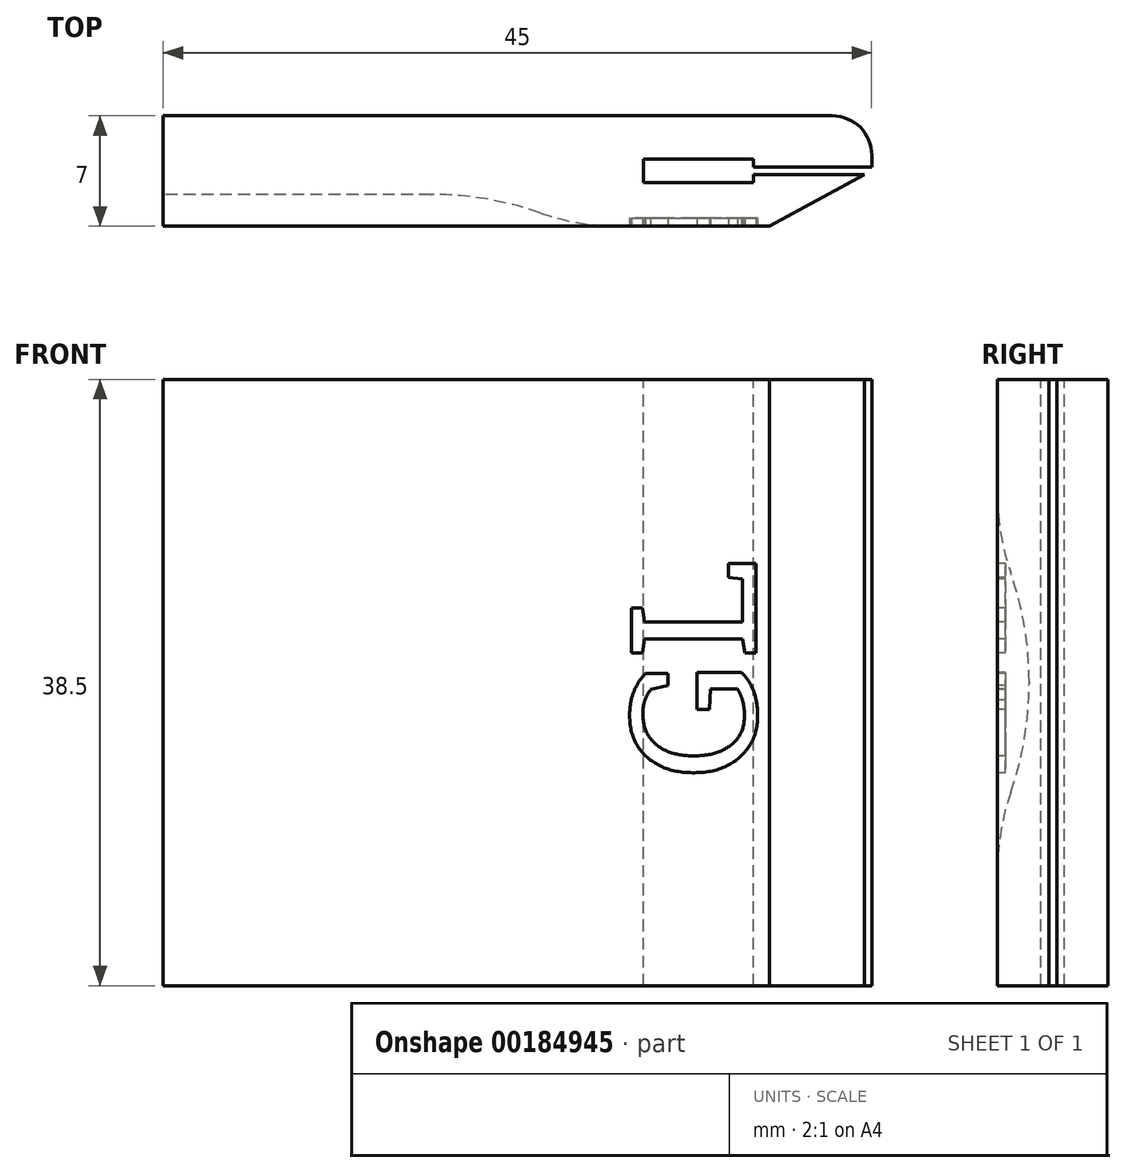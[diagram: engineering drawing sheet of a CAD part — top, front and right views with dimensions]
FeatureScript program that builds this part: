
annotation { "Feature Type Name" : "Feature", "Feature Type Description" : "" }
export const myFeature = defineFeature(function(context is Context, id is Id, definition is map)
    precondition{}
    {
        {
            var Q0;
            Q0=qCreatedBy(makeId("Top.planeOp"),FACE);
            var sketch = newSketch(context, id + "F0", { "sketchPlane" : qUnion([Q0])});
            skLineSegment(sketch, "E0.bottom", {"start": v(-22.94, 8.97) * mm, "end": v(22.06, 8.97) * mm});
            skLineSegment(sketch, "E0.top", {"start": v(-22.94, 1.97) * mm, "end": v(22.06, 1.97) * mm});
            skLineSegment(sketch, "E0.left", {"start": v(-22.94, 8.97) * mm, "end": v(-22.94, 1.97) * mm});
            skLineSegment(sketch, "E0.right", {"start": v(22.06, 8.97) * mm, "end": v(22.06, 1.97) * mm});
            skSolve(sketch);
        }
        {
            var Q0;
            Q0=makeQuery(id+"F0.imprint","IMPRINT",FACE,{"disambiguationData":[TD([[makeQuery(id+"F0.imprint","IMPRINT",EDGE,{"derivedFrom":sQuery(id+"F0.wireOp",EDGE,"E0.bottom")}),-1.0]])]});
            extrude(context, id + "F1", {"entities" : qUnion([Q0]), "depth" : 38.5 * mm});
        }
        {
            var Q0;
            Q0=makeQuery(id+"F1.opExtrude","SWEPT_EDGE",EDGE,{"disambiguationData":[OSD([sQuery(id+"F0.wireOp",EDGE,"E0.top"),sQuery(id+"F0.wireOp",EDGE,"E0.right")])]});
            chamfer(context, id + "F2", {"entities" : qUnion([Q0]), "chamferType" : ChamferType.TWO_OFFSETS, "width1" : 3.5 * mm, "oppositeDirection" : false, "width2" : 6.5 * mm, "tangentPropagation" : true});
        }
        {
            var Q0;
            Q0=makeQuery(id+"F1.opExtrude","SWEPT_EDGE",EDGE,{"disambiguationData":[OSD([sQuery(id+"F0.wireOp",EDGE,"E0.bottom"),sQuery(id+"F0.wireOp",EDGE,"E0.right")])]});
            fillet(context, id + "F3", {"entities" : qUnion([Q0]), "radius" : 2.5 * mm, "tangentPropagation" : true, "allowEdgeOverflow" : false});
        }
        {
            var Q0;
            Q0=makeQuery(id+"F1.opExtrude","SWEPT_FACE",FACE,{"disambiguationData":[OSD([sQuery(id+"F0.wireOp",EDGE,"E0.top")])]});
            var sketch = newSketch(context, id + "F4", { "sketchPlane" : qUnion([Q0])});
            skLineSegment(sketch, "E1.bottom", {"start": v(-22.94, 28.25) * mm, "end": v(3.06, 28.25) * mm});
            skLineSegment(sketch, "E1.top", {"start": v(-22.94, 10.25) * mm, "end": v(3.06, 10.25) * mm});
            skLineSegment(sketch, "E1.left", {"start": v(-22.94, 28.25) * mm, "end": v(-22.94, 10.25) * mm});
            skLineSegment(sketch, "E1.right", {"start": v(3.06, 28.25) * mm, "end": v(3.06, 10.25) * mm});
            skLineSegment(sketch, "E2", {"start": v(3.06, 19.25) * mm, "end": v(-22.94, 19.25) * mm, "construction": true});
            skSolve(sketch);
        }
        {
            var Q0;
            Q0=makeQuery(id+"F4.imprint","IMPRINT",FACE,{"disambiguationData":[TD([[makeQuery(id+"F4.imprint","IMPRINT",EDGE,{"derivedFrom":sQuery(id+"F4.wireOp",EDGE,"E1.bottom")}),-1.0]])]});
            extrude(context, id + "F5", {"entities" : qUnion([Q0]), "operationType" : NewBodyOperationType.REMOVE, "oppositeDirection" : true, "depth" : 2 * mm});
        }
        {
            var Q0;
            Q0=makeQuery(id+"F5.boolean.opBoolean","COPY",EDGE,{"derivedFrom":makeQuery(id+"F5.opExtrude","SWEPT_EDGE",EDGE,{"disambiguationData":[OSD([sQuery(id+"F4.wireOp",EDGE,"E1.bottom"),sQuery(id+"F4.wireOp",EDGE,"E1.right")])]})});
            var Q1;
            Q1=makeQuery(id+"F5.boolean.opBoolean","COPY",EDGE,{"derivedFrom":makeQuery(id+"F5.opExtrude","SWEPT_EDGE",EDGE,{"disambiguationData":[OSD([sQuery(id+"F4.wireOp",EDGE,"E1.top"),sQuery(id+"F4.wireOp",EDGE,"E1.right")])]})});
            fillet(context, id + "F6", {"entities" : qUnion([Q0, Q1]), "radius" : 9 * mm, "tangentPropagation" : true, "allowEdgeOverflow" : false});
        }
        {
            var Q0;
            Q0=makeQuery(id+"F5.boolean.opBoolean","COPY",EDGE,{"derivedFrom":makeQuery(id+"F5.opExtrude","CAP_EDGE",EDGE,{"disambiguationData":[OSD([sQuery(id+"F4.wireOp",EDGE,"E1.top")])],"isStart":false})});
            fillet(context, id + "F7", {"entities" : qUnion([Q0]), "radius" : 21 * mm, "tangentPropagation" : true, "allowEdgeOverflow" : false});
        }
        {
            var Q0;
            Q0=makeQuery(id+"F1.opExtrude","SWEPT_FACE",FACE,{"disambiguationData":[OSD([sQuery(id+"F0.wireOp",EDGE,"E0.top")])]});
            var Q1;
            Q1=makeQuery(id+"F1.opExtrude","SWEPT_FACE",FACE,{"disambiguationData":[OSD([sQuery(id+"F0.wireOp",EDGE,"E0.bottom")])]});
            cPlane(context, id + "F8", {"entities" : qUnion([Q0, Q1]), "cplaneType" : CPlaneType.MID_PLANE, "offset" : 25 * mm, "width" : 150 * mm, "height" : 150 * mm});
        }
        {
            var Q0;
            Q0=makeQuery(id+"F1.opExtrude","CAP_FACE",FACE,{"disambiguationData":[OSD([sQuery(id+"F0.wireOp",EDGE,"E0.bottom"),sQuery(id+"F0.wireOp",EDGE,"E0.top"),sQuery(id+"F0.wireOp",EDGE,"E0.left"),sQuery(id+"F0.wireOp",EDGE,"E0.right")])],"isStart":false});
            var sketch = newSketch(context, id + "F9", { "sketchPlane" : qUnion([Q0])});
            skLineSegment(sketch, "E3.bottom", {"start": v(14.56, 5.72) * mm, "end": v(22.06, 5.72) * mm});
            skLineSegment(sketch, "E3.top", {"start": v(14.56, 5.22) * mm, "end": v(22.06, 5.22) * mm});
            skLineSegment(sketch, "E3.left", {"start": v(14.56, 5.72) * mm, "end": v(14.56, 5.22) * mm});
            skLineSegment(sketch, "E3.right", {"start": v(22.06, 5.72) * mm, "end": v(22.06, 5.22) * mm});
            skLineSegment(sketch, "E4.bottom", {"start": v(7.56, 6.22) * mm, "end": v(14.56, 6.22) * mm});
            skLineSegment(sketch, "E4.top", {"start": v(7.56, 4.72) * mm, "end": v(14.56, 4.72) * mm});
            skLineSegment(sketch, "E4.left", {"start": v(7.56, 6.22) * mm, "end": v(7.56, 4.72) * mm});
            skLineSegment(sketch, "E4.right", {"start": v(14.56, 6.22) * mm, "end": v(14.56, 4.72) * mm});
            skSolve(sketch);
        }
        {
            var Q0;
            {var subQ3=sQuery(id+"F9.wireOp",EDGE,"E4.bottom");Q0=makeQuery(id+"F9.imprint","IMPRINT",FACE,{"disambiguationData":[TD([[makeQuery(id+"F9.imprint","IMPRINT",EDGE,{"derivedFrom":subQ3}),-1.0]])]});}
            var Q1;
            {var subQ5=sQuery(id+"F9.wireOp",EDGE,"E3.bottom");Q1=makeQuery(id+"F9.imprint","IMPRINT",FACE,{"disambiguationData":[TD([[makeQuery(id+"F9.imprint","IMPRINT",EDGE,{"derivedFrom":subQ5}),-1.0]])]});}
            extrude(context, id + "F10", {"entities" : qUnion([Q0, Q1]), "operationType" : NewBodyOperationType.REMOVE, "endBound" : BoundingType.UP_TO_NEXT, "oppositeDirection" : true, "depth" : 25 * mm});
        }
        {
            var Q0;
            Q0=makeQuery(id+"F7.opFillet","BLEND_EDGE",EDGE,{"disambiguationData":[OD(0.0)],"blendedFrom":[makeQuery(id+"F5.boolean.opBoolean","COPY",EDGE,{"derivedFrom":makeQuery(id+"F5.opExtrude","CAP_EDGE",EDGE,{"disambiguationData":[OSD([sQuery(id+"F4.wireOp",EDGE,"E1.bottom")])],"isStart":false})}),makeQuery(id+"F1.opExtrude","SWEPT_FACE",FACE,{"disambiguationData":[OSD([sQuery(id+"F0.wireOp",EDGE,"E0.top")])]})],"blendedInto":[makeQuery(id+"F1.opExtrude","SWEPT_FACE",FACE,{"disambiguationData":[OSD([sQuery(id+"F0.wireOp",EDGE,"E0.top")])]})]});
            var Q1;
            Q1=makeQuery(id+"FHQU1zlOLmeoFjk_1.1.F7.opFillet","BLEND_EDGE",EDGE,{"blendedFrom":[makeQuery(id+"FHQU1zlOLmeoFjk_1.1.F5.boolean.opBoolean","COPY",EDGE,{"derivedFrom":makeQuery(id+"FHQU1zlOLmeoFjk_1.1.F5.opExtrude","CAP_EDGE",EDGE,{"disambiguationData":[OSD([sQuery(id+"F4.wireOp",EDGE,"E1.bottom")])],"isStart":false})}),makeQuery(id+"F1.opExtrude","SWEPT_FACE",FACE,{"disambiguationData":[OSD([sQuery(id+"F0.wireOp",EDGE,"E0.bottom")])]})],"blendedInto":[makeQuery(id+"F1.opExtrude","SWEPT_FACE",FACE,{"disambiguationData":[OSD([sQuery(id+"F0.wireOp",EDGE,"E0.bottom")])]})]});
            fillet(context, id + "F11", {"entities" : qUnion([Q0, Q1]), "radius" : 15 * mm, "tangentPropagation" : true, "allowEdgeOverflow" : false});
        }
        {
            var Q0;
            Q0=makeQuery(id+"F1.opExtrude","SWEPT_FACE",FACE,{"disambiguationData":[OSD([sQuery(id+"F0.wireOp",EDGE,"E0.top")])]});
            var sketch = newSketch(context, id + "F12", { "sketchPlane" : qUnion([Q0])});
            skText(sketch, "E5", { "text": "GL\n", "fontName": "RobotoSlab-Regular.ttf"});
            const initialGuessF12  = {"E5": [0.0147, 0.01323, 0, 1, 0.008]};
            skSetInitialGuess(sketch, initialGuessF12);
            skSolve(sketch);
        }
        {
            var Q0;
            Q0=makeQuery(id+"F12.imprint","IMPRINT",FACE,{"disambiguationData":[TD([[makeQuery(id+"F12.imprint","IMPRINT",EDGE,{"derivedFrom":sQuery(id+"F12.wireOp",EDGE,"E5.sketch_text.stroke-0")}),-1.0]])]});
            var Q1;
            Q1=makeQuery(id+"F12.imprint","IMPRINT",FACE,{"disambiguationData":[TD([[makeQuery(id+"F12.imprint","IMPRINT",EDGE,{"derivedFrom":sQuery(id+"F12.wireOp",EDGE,"E5.sketch_text.stroke-26")}),-1.0]])]});
            extrude(context, id + "F13", {"entities" : qUnion([Q0, Q1]), "operationType" : NewBodyOperationType.REMOVE, "oppositeDirection" : true, "depth" : .5 * mm});
        }
    });
